# Revit family: IS_Contour21_S2412_BIM_DE
name_source: partatom
category: Plumbing Fixtures
revit_build: Autodesk Revit MEP 2016 (Build: 20161004_0715(x64)
units: mm (PartAtom-declared; Revit-internal decimal feet)

## family parameters
Cut with Voids When Loaded = No
Host = Face
OmniClass Number = 23.45.05.14.14
OmniClass Title = Sinks/Lavatories
Part Type = Normal
Room Calculation Point = No
Round Connector Dimension = Use Diameter
Shared = No

## types (2) — shared parameters
Accessories = www.idealstandard.de\ersatzteile
AreaUnits = millimeters
Assembly Code = C1030200
AssetType = Fixed
BIMobject category = Basins
Brand = Ideal Standard
Brand url = http://www.idealstandard.co.uk
CodePerformance = DIN EN 14688 CL 00, DIN EN 31, DIN
Color = White
ConnectionType = Plumbing
CurrencyUnit = €
Date of publishing = 5/15/2017
Default Elevation = 850 mm
Description = CONTOUR 21 UMYVADLO 50 CM, BEZ PŘEPADU
DurationUnit = year
Edition number = 1
ExpectedLife = 25
Features = CONTOUR21 handrinse washbasin 500x420mm, 1 taphole, no overflow
GrossWeight = 9,708 kg
IFC Classification = Sanitary Terminal
Installation instructions = http://www.idealstandard.de
InstallationDate = 1900-12-31T23:59:59
InstallationInstructions = www.idealstandard.de\produkte
LinearUnits = millimeters
Manufacturer name = Ideal Standard
ManufacturerURL = www.idealstandard.de
Material = Vitreous china
Material main = Ceramics
NBS Reference Code = 35-79-94
NBS Reference Description = Wall-Hung Wash Basins
Nominal height = 195 mm
Nominal width = 500 mm
NominalLength = 420 mm
Product Guid = ff4bd6dd-2720-41df-9fd1-8ca79a0c425f
Product SKU = S2412
Product data url = https://bimobject.com
Product family = CONTOUR 21
Product group = Basin
Product url = http://www.idealstandard.de
ProductInformation = www.idealstandard.de
QR code = http://bimobject.com
Shape = Sculptured
Size = 500 x 420 x 195 mm
Space = Internal
Technical description = http://www.idealstandard.de
URL = www.idealstandard.de
Uniclass 2.0 Code = PR-35-79-94
Uniclass 2.0 Description = Wall-Hung Wash Basins
Uniclass 2015 Code = Pr_40_20_96_96
Uniclass 2015 Name = Wall-hung wash basins
Uniclass2015Code = Pr_40_20_96_81
Uniclass2015Title = Sinks
Uniclass2015Version = Products v1.1
Version = 1
VolumeUnits = Litres
Weight Net (Kg) = 9.61
zero-valued in all types: Cost, NominalDepth

## per-type parameters (varying)
| type | BIMObjectName | BarCode | EAN code | Finish | Model | ModelNumber | ModelReference | Name |
| S241201 - CONTOUR21 handrinse washbasin 500x420mm, 1 taphole, no overflow | ISI_IdealStandard_Sinks_CONTOUR 21_S241201 | 5017830398844 | https://5017830398844 | White | S241201 | S241201 | IS Handwaschbecken CONTOUR 21, 1 Hl., o.Ül., 500x420x195mm, Weiß | ISI_IdealStandard_Sinks_CONTOUR 21_S241201 |
| S2412MA - CONTOUR21 handrinse washbasin 500x420mm, 1 taphole, no overflow | ISI_IdealStandard_Sinks_CONTOUR 21_S2412MA | 5017830506683 | https://5017830506683 | White IP | S2412MA | S2412MA | IS Handwaschbecken CONTOUR 21, 1 Hl., o.Ül., 500x420x195mm, Weiß m.Ideal Plus | ISI_IdealStandard_Sinks_CONTOUR 21_S2412MA |

## geometry (parser evidence)
native form markers: Blend x2, Sweep x3
no freeform markers — native parametric forms only
